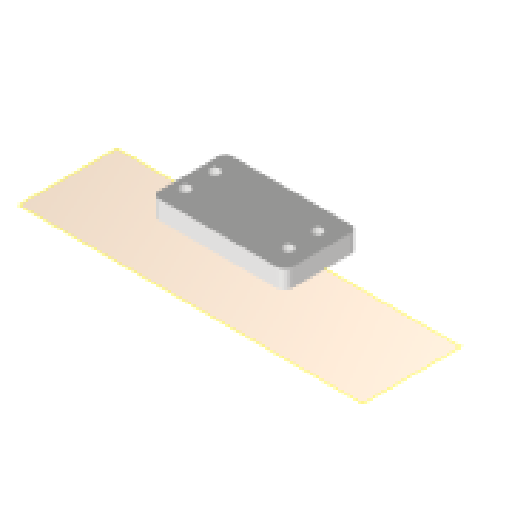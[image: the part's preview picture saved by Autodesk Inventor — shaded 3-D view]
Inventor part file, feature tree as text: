
AUTODESK INVENTOR PART (.ipt)
format: ipt  version: 2024.1 (Build 281209000, 209)  size: 120,320 bytes
history: native  units: mm
features: other x3, reference x2, plane x1, extrude x1, fillet x1, mirror x1, sketch x1
ambient origin geometry x8: Origin, YZ Plane, XZ Plane, XY Plane, X Axis, Y Axis, Z Axis, Center Point
bodies: Volumenkörper1 (feature_tree)
feature tree (10):
  plane  "Arbeitsebene1"
  extrude  "Extrusion1"  Depth=10.0mm
  fillet  "Rundung1"  Radius=3.0mm
  mirror  "Spiegeln1"
  sketch  "Skizze1"  dims[d0=36.0mm d1=10.0mm d2=3.0mm d3=5.0mm d4=0.0mm d5=2.0mm]
  reference  "Referenz1"
  reference  "Referenz2"
  other  "Assembly_Planktoscope_Uc2version_wormdrive_V3.iam"
  other  "60_Planktoscope_Base_half_wormdrive_1:2"
  other  "60_Planktoscope_Base_half1_MIR:1"
